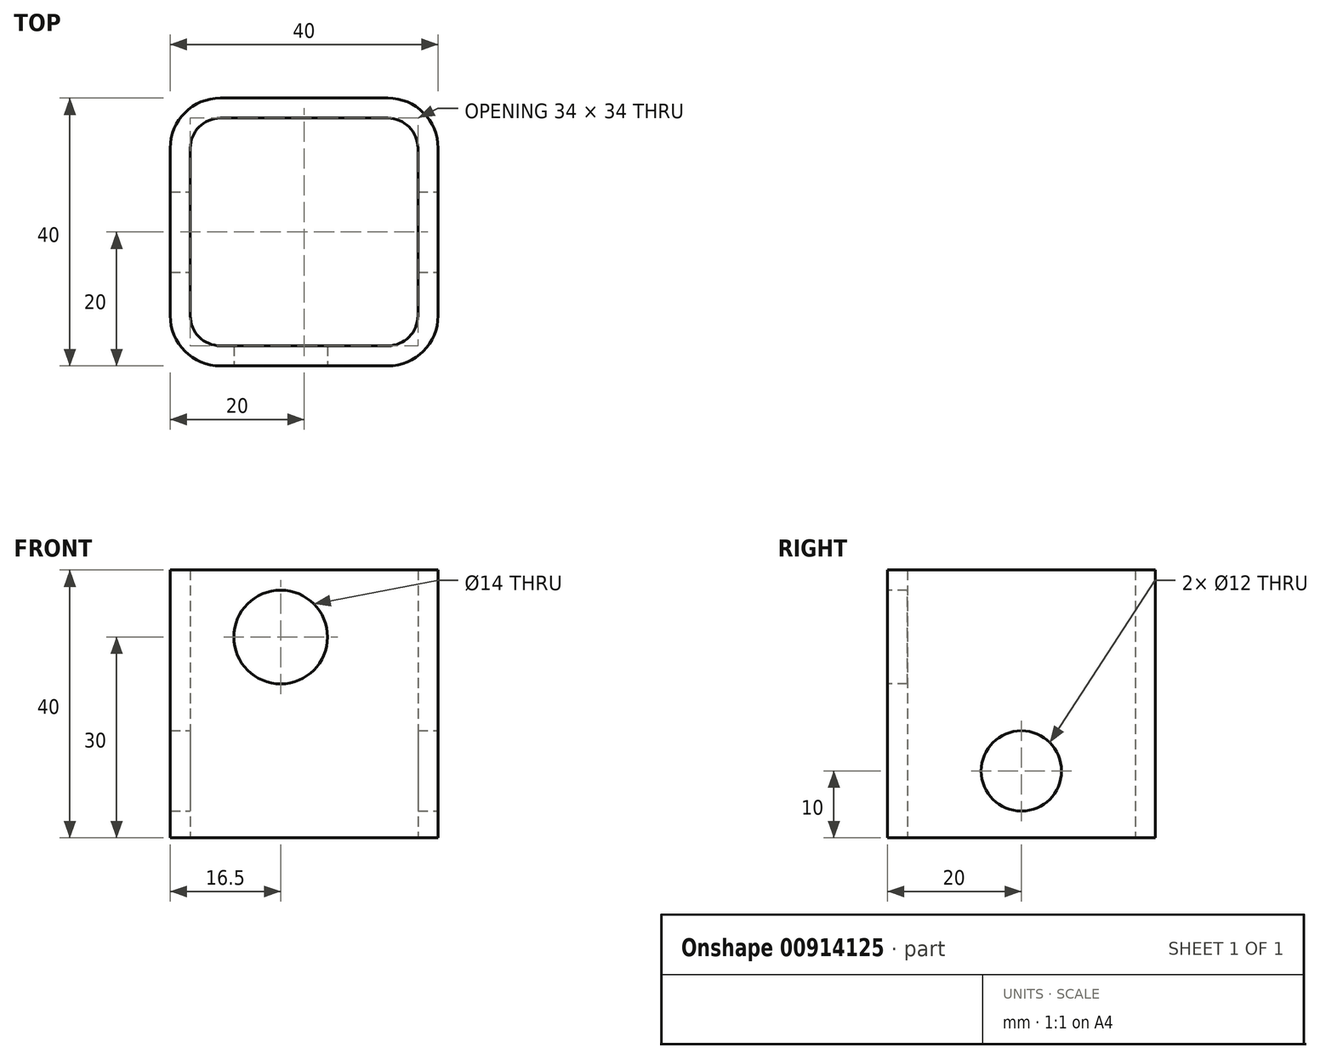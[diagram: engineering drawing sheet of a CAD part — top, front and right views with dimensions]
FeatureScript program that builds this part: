
annotation { "Feature Type Name" : "Feature", "Feature Type Description" : "" }
export const myFeature = defineFeature(function(context is Context, id is Id, definition is map)
    precondition{}
    {
        {
            var Q0;
            Q0=qCreatedBy(makeId("Top.planeOp"),FACE);
            var sketch = newSketch(context, id + "F0", { "sketchPlane" : qUnion([Q0])});
            skLineSegment(sketch, "E0.bottom", {"start": v(12.5, -20) * mm, "end": v(-12.5, -20) * mm});
            skLineSegment(sketch, "E0.top", {"start": v(12.5, 20) * mm, "end": v(-12.5, 20) * mm});
            skLineSegment(sketch, "E0.left", {"start": v(20, -12.5) * mm, "end": v(20, 12.5) * mm});
            skLineSegment(sketch, "E0.right", {"start": v(-20, -12.5) * mm, "end": v(-20, 12.5) * mm});
            skPoint(sketch, "E0.middle", {"position": v(0, 0) * mm});
            skPoint(sketch, "E1.visualSharp", {"position": v(20, 20) * mm});
            skArc(sketch, "E1.filletArc", {"start": v(20, 12.5) * mm, "mid": v(17.8, 17.8) * mm, "end": v(12.5, 20) * mm});
            skPoint(sketch, "E2.visualSharp", {"position": v(-20, 20) * mm});
            skArc(sketch, "E2.filletArc", {"start": v(-12.5, 20) * mm, "mid": v(-17.8, 17.8) * mm, "end": v(-20, 12.5) * mm});
            skPoint(sketch, "E3.visualSharp", {"position": v(-20, -20) * mm});
            skArc(sketch, "E3.filletArc", {"start": v(-20, -12.5) * mm, "mid": v(-17.8, -17.8) * mm, "end": v(-12.5, -20) * mm});
            skPoint(sketch, "E4.visualSharp", {"position": v(20, -20) * mm});
            skArc(sketch, "E4.filletArc", {"start": v(12.5, -20) * mm, "mid": v(17.8, -17.8) * mm, "end": v(20, -12.5) * mm});
            skLineSegment(sketch, "E5.0", {"start": v(-17, -12.5) * mm, "end": v(-17, 12.5) * mm});
            skArc(sketch, "E5.1", {"start": v(-12.5, 17) * mm, "mid": v(-15.68, 15.68) * mm, "end": v(-17, 12.5) * mm});
            skArc(sketch, "E5.2", {"start": v(-17, -12.5) * mm, "mid": v(-15.68, -15.68) * mm, "end": v(-12.5, -17) * mm});
            skLineSegment(sketch, "E5.3", {"start": v(12.5, 17) * mm, "end": v(-12.5, 17) * mm});
            skLineSegment(sketch, "E5.4", {"start": v(12.5, -17) * mm, "end": v(-12.5, -17) * mm});
            skArc(sketch, "E5.5", {"start": v(12.5, -17) * mm, "mid": v(15.68, -15.68) * mm, "end": v(17, -12.5) * mm});
            skLineSegment(sketch, "E5.6", {"start": v(17, -12.5) * mm, "end": v(17, 12.5) * mm});
            skArc(sketch, "E5.7", {"start": v(17, 12.5) * mm, "mid": v(15.68, 15.68) * mm, "end": v(12.5, 17) * mm});
            skSolve(sketch);
        }
        {
            var Q0;
            Q0 = qSketchRegion(id + "F0", true);
            extrude(context, id + "F1", {"entities" : qUnion([Q0]), "depth" : 40 * mm, "offsetDistance" : 25 * mm});
        }
        {
            var Q0;
            Q0=makeQuery(id+"F1.opExtrude","SWEPT_FACE",FACE,{"disambiguationData":[OSD([sQuery(id+"F0.wireOp",EDGE,"E0.bottom")])]});
            var sketch = newSketch(context, id + "F2", { "sketchPlane" : qUnion([Q0])});
            skPoint(sketch, "E6", {"position": v(-3.5, 30) * mm});
            skSolve(sketch);
        }
        {
            var Q0;
            Q0=sQuery(id+"F2.wireOp",VERTEX,"E6");
            var Q1;
            Q1=makeQuery(id+"F1.opExtrude","SWEPT_BODY",BODY,{"disambiguationData":[OSD([sQuery(id+"F0.wireOp",EDGE,"E0.bottom"),sQuery(id+"F0.wireOp",EDGE,"E0.top"),sQuery(id+"F0.wireOp",EDGE,"E0.left"),sQuery(id+"F0.wireOp",EDGE,"E0.right"),sQuery(id+"F0.wireOp",EDGE,"E1.filletArc"),sQuery(id+"F0.wireOp",EDGE,"E2.filletArc"),sQuery(id+"F0.wireOp",EDGE,"E3.filletArc"),sQuery(id+"F0.wireOp",EDGE,"E4.filletArc"),sQuery(id+"F0.wireOp",EDGE,"E5.0"),sQuery(id+"F0.wireOp",EDGE,"E5.1"),sQuery(id+"F0.wireOp",EDGE,"E5.2"),sQuery(id+"F0.wireOp",EDGE,"E5.3"),sQuery(id+"F0.wireOp",EDGE,"E5.4"),sQuery(id+"F0.wireOp",EDGE,"E5.5"),sQuery(id+"F0.wireOp",EDGE,"E5.6"),sQuery(id+"F0.wireOp",EDGE,"E5.7")])]});
            hole(context, id + "F3", {"style" : HoleStyle.SIMPLE, "endStyle" : HoleEndStyle.BLIND, "standardTappedOrClearance" : lookupTablePath({ "standard" : "ISO", "size" : "14", "type" : "Drilled" }), "standardBlindInLast" : lookupTablePath({ "standard" : "ISO", "size" : "14", "type" : "Drilled" }), "holeDiameter" : 14 * mm, "majorDiameter" : 16 * mm, "holeDepth" : 3 * mm, "tappedDepth" : 14 * mm, "tapClearance" : 3, "locations" : qUnion([Q0]), "scope" : qUnion([Q1])});
        }
        {
            var Q0;
            Q0=makeQuery(id+"F1.opExtrude","SWEPT_FACE",FACE,{"disambiguationData":[OSD([sQuery(id+"F0.wireOp",EDGE,"E0.left")])]});
            var sketch = newSketch(context, id + "F4", { "sketchPlane" : qUnion([Q0])});
            skPoint(sketch, "E7", {"position": v(0, 10) * mm});
            skSolve(sketch);
        }
        {
            var Q0;
            Q0=sQuery(id+"F4.wireOp",VERTEX,"E7");
            var Q1;
            Q1=makeQuery(id+"F1.opExtrude","SWEPT_BODY",BODY,{"disambiguationData":[OSD([sQuery(id+"F0.wireOp",EDGE,"E0.bottom"),sQuery(id+"F0.wireOp",EDGE,"E0.top"),sQuery(id+"F0.wireOp",EDGE,"E0.left"),sQuery(id+"F0.wireOp",EDGE,"E0.right"),sQuery(id+"F0.wireOp",EDGE,"E1.filletArc"),sQuery(id+"F0.wireOp",EDGE,"E2.filletArc"),sQuery(id+"F0.wireOp",EDGE,"E3.filletArc"),sQuery(id+"F0.wireOp",EDGE,"E4.filletArc"),sQuery(id+"F0.wireOp",EDGE,"E5.0"),sQuery(id+"F0.wireOp",EDGE,"E5.1"),sQuery(id+"F0.wireOp",EDGE,"E5.2"),sQuery(id+"F0.wireOp",EDGE,"E5.3"),sQuery(id+"F0.wireOp",EDGE,"E5.4"),sQuery(id+"F0.wireOp",EDGE,"E5.5"),sQuery(id+"F0.wireOp",EDGE,"E5.6"),sQuery(id+"F0.wireOp",EDGE,"E5.7")])]});
            hole(context, id + "F5", {"style" : HoleStyle.SIMPLE, "endStyle" : HoleEndStyle.THROUGH, "standardTappedOrClearance" : lookupTablePath({ "standard" : "ISO", "size" : "12", "type" : "Drilled" }), "standardBlindInLast" : lookupTablePath({ "standard" : "ISO", "size" : "12", "type" : "Drilled" }), "holeDiameter" : 12 * mm, "majorDiameter" : 5 * mm, "tappedDepth" : 14 * mm, "tapClearance" : 3, "locations" : qUnion([Q0]), "scope" : qUnion([Q1])});
        }
    });
